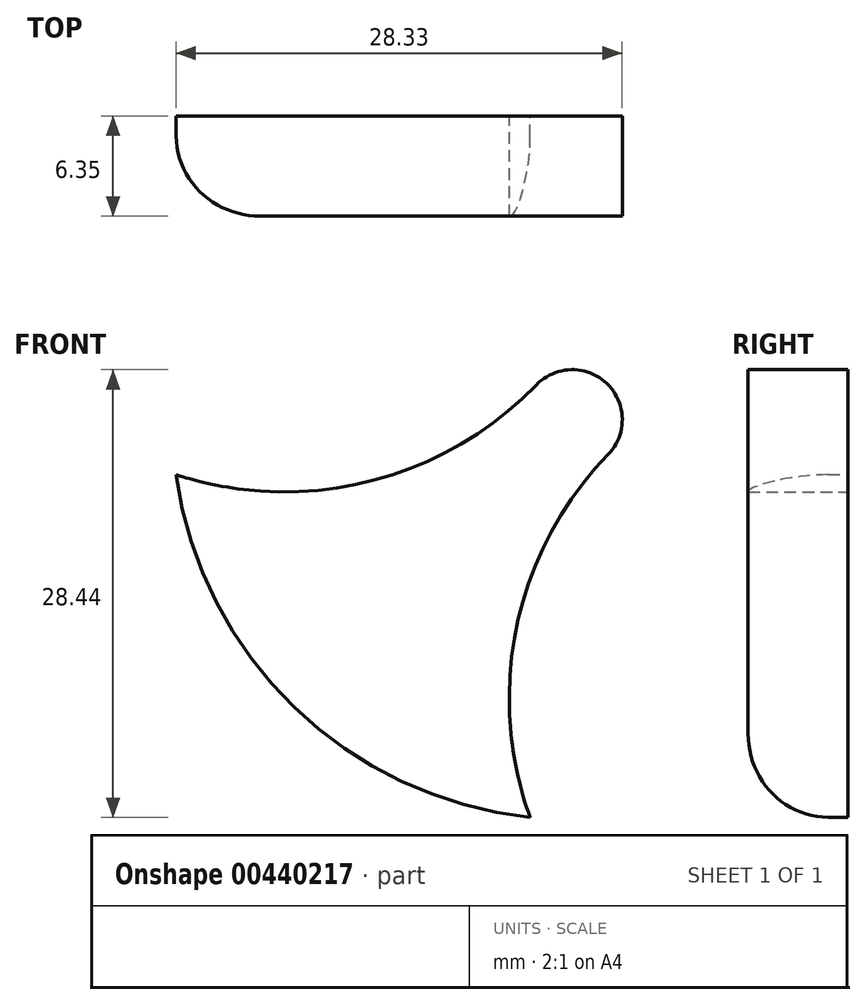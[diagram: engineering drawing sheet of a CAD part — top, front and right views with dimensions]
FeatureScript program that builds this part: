
annotation { "Feature Type Name" : "Feature", "Feature Type Description" : "" }
export const myFeature = defineFeature(function(context is Context, id is Id, definition is map)
    precondition{}
    {
        {
            var Q0;
            Q0=qCreatedBy(makeId("Front.planeOp"),FACE);
            var sketch = newSketch(context, id + "F0", { "sketchPlane" : qUnion([Q0])});
            skCircle(sketch, "E0", {"center": v(0, 0) * mm, "radius": 25.4 * mm});
            skCircle(sketch, "E1", {"center": v(0, 0) * mm, "radius": 3.18 * mm});
            skCircle(sketch, "E2", {"center": v(-18.28, 17.64) * mm, "radius": 22.22 * mm});
            skCircle(sketch, "E3", {"center": v(18.22, -17.7) * mm, "radius": 22.22 * mm});
            skCircle(sketch, "E4", {"center": v(18.28, 17.64) * mm, "radius": 22.22 * mm});
            skSolve(sketch);
        }
        {
            var Q0;
            {var subQ0=sQuery(id+"F0.wireOp",EDGE,"E2");var subQ1=sQuery(id+"F0.wireOp",EDGE,"E0");var subQ2=makeQuery(id+"F0.imprint","INTERSECT",VERTEX,{"disambiguationData":[OD(0.0)],"derivedFrom":[subQ1,subQ0]});Q0=makeQuery(id+"F0.imprint","IMPRINT",FACE,{"disambiguationData":[TD([[makeQuery(id+"F0.imprint","IMPRINT",EDGE,{"disambiguationData":[TD([[subQ2,-1.0]])],"derivedFrom":subQ1}),1.0]])]});}
            var Q1;
            {var subQ0=sQuery(id+"F0.wireOp",EDGE,"E1");var subQ1=makeQuery(id+"F0.imprint","INTERSECT",VERTEX,{"derivedFrom":[subQ0,sQuery(id+"F0.wireOp",EDGE,"E2")]});Q1=makeQuery(id+"F0.imprint","IMPRINT",FACE,{"disambiguationData":[TD([[makeQuery(id+"F0.imprint","IMPRINT",EDGE,{"disambiguationData":[TD([[subQ1,1.0]])],"derivedFrom":subQ0}),1.0]])]});}
            extrude(context, id + "F1", {"entities" : qUnion([Q0, Q1]), "depth" : 6.35 * mm});
        }
        {
            var Q0;
            Q0=makeQuery(id+"F1.opExtrude","CAP_EDGE",EDGE,{"disambiguationData":[OSD([sQuery(id+"F0.wireOp",EDGE,"E0")])],"isStart":false});
            fillet(context, id + "F2", {"entities" : qUnion([Q0]), "radius" : 5.08 * mm, "tangentPropagation" : true, "allowEdgeOverflow" : false});
        }
    });
